# Revit family: PRD_FrankeWS_JntrlUnits_SiriusMultiPurposeSink_SIRX757
name_source: partatom
category: Plumbing Fixtures
revit_build: Autodesk Revit 2018 (Build: 20190510_1515(x64)
units: mm (PartAtom-declared; Revit-internal decimal feet)

## family parameters
Always vertical = Yes
Cut with Voids When Loaded = No
OmniClass Number = 23.45.05.14.14
OmniClass Title = Sinks/Lavatories
Part Type = Normal
Room Calculation Point = No
Round Connector Dimension = Use Diameter
Shared = No
Work Plane-Based = No

## types (1)
- SIRX757
    AssetType = Movable
    BIMObjectName = PRD_AR_JanitorialUnits_SiriusMultiPurposeSink_SIRX757
    Category = Pr_40_20_96_44, Janitorial sinks
    Color = Stainless steel
    Description = Sludge trap sink, stainless steel, surface satin finished, material thickness 1.2 mm, on rollers with break device. with 2'' waste and connected PVC pipe as overflow.
    DrainSize = DN-50-2INH
    DurationUnit = year
    Features = stainless steel, 1.20 mm, satin finished, no mounting, 600x360x550 mm (WxHxD)
    Finish = Satin finished
    FinishAndMaterial = Stainless steel 1.4301
    Form = Stainless steel multi purpose sink
    GrossWeight = 14.90 kg
    IfcExportAs = IfcSanitaryTerminalType
    IfcExportType = SINK
    Manufacturer = KWC Group AG
    ManufacturerName = KWC Group AG
    ManufacturerURL = www.kwc.com
    Material = Stainless steel
    Model = SIRX757
    ModelNumber = 2000100363
    ModelReference = SIRX757
    NBSDescription = Janitorial units
    NBSReference = 45-35-70/401
    Name = Sirius multi purpose sink SIRX757
    NetWeight = 13.00 kg
    NominalDepth = 550 mm  [stored 1.80446 ft]
    NominalHeight = 360 mm  [stored 1.1811 ft]
    NominalLength = 0 mm  [stored 0 ft]
    NominalWidth = 600 mm
    PipeMaterial = <By Category>
    ProductInformation = https://pim.kwc.com
    RolerMaterial = <By Category>
    Shape = Rectangular
    SinkMaterial = PRD_AR_StainlessSteel_SatinFinished
    SinkMounting = Other
    SinkType = Other
    Size = 600 x 550 x 360 mm
    URL = www.kwc.com
    Uniclass2015Code = Pr_40_20_96_44
    Uniclass2015Title = Janitorial sinks
    Uniclass2015Version = Products v1.5
    Version = 1
    WarrantyDurationUnit = year
    WaterSupplyOverflowAndWasteHolesOverflow = Yes
    WaterSupplyOverflowAndWasteHolesWaste = No
    WaterSupplyOverflowAndWasteHolesWaterSupply = No tapholes

note: [stored X ft] marks values corroborated as IEEE doubles in the binary element streams (Revit-internal decimal feet)

## geometry (parser evidence)
native form markers: Sweep x5
no freeform markers — native parametric forms only
